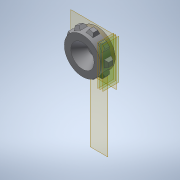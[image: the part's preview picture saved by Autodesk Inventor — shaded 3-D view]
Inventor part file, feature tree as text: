
AUTODESK INVENTOR PART (.ipt)
format: ipt  version: 2020 (Build 240168000, 168)  size: 204,800 bytes
history: native  units: mm
features: other x12, sketch x6, extrude x4, loft x1, pattern_circular x1, chamfer x1, reference x1
ambient origin geometry x8: Origin, YZ Plane, XZ Plane, XY Plane, X Axis, Y Axis, Z Axis, Center Point
bodies: Body1 (feature_tree)
feature tree (26):
  other  "Bryła1"
  other  "Płaszczyzna konstrukcyjna1"
  extrude  "Wyciągnięcie proste1"  Depth=20.0mm
  other  "Płaszczyzna konstrukcyjna2"
  extrude  "Wyciągnięcie proste2"  Depth=50.0mm
  extrude  "Wyciągnięcie proste3"  Depth=20.0mm TaperAngle=0.0deg
  other  "Płaszczyzna konstrukcyjna4"
  other  "Płaszczyzna konstrukcyjna5"
  sketch  "Szkic5"
  other  "Płaszczyzna konstrukcyjna6"
  loft  "Wyciągnięcie złożone1"
  pattern_circular  "Szyk kołowy1"  [2 undecoded]
  extrude  "Wyciągnięcie proste4"  TaperAngle=0.0deg  [1 undecoded]
  chamfer  "Faza2"  Distance=3.0mm
  sketch  "Szkic1"
  reference  "Odniesienie1"
  sketch  "Szkic3"
  sketch  "Szkic4"
  other  "Płaszczyzna konstrukcyjna3"
  sketch  "Szkic6"
  sketch  "Szkic7"
  other  "<userpath>\Desktop\3d\scanning-robot\Assembly1.iam"
  other  "Assembly1.iam"
  other  "Tower Pro MG90S Micro servo:2"
  other  "Крышка корпуса:1"
  other  "base:1"
note: 3 required parameter values undecoded (feature->parameter linkage not recoverable at this tier; creation-order binding heuristic only, values carry confidence <= 0.55)
